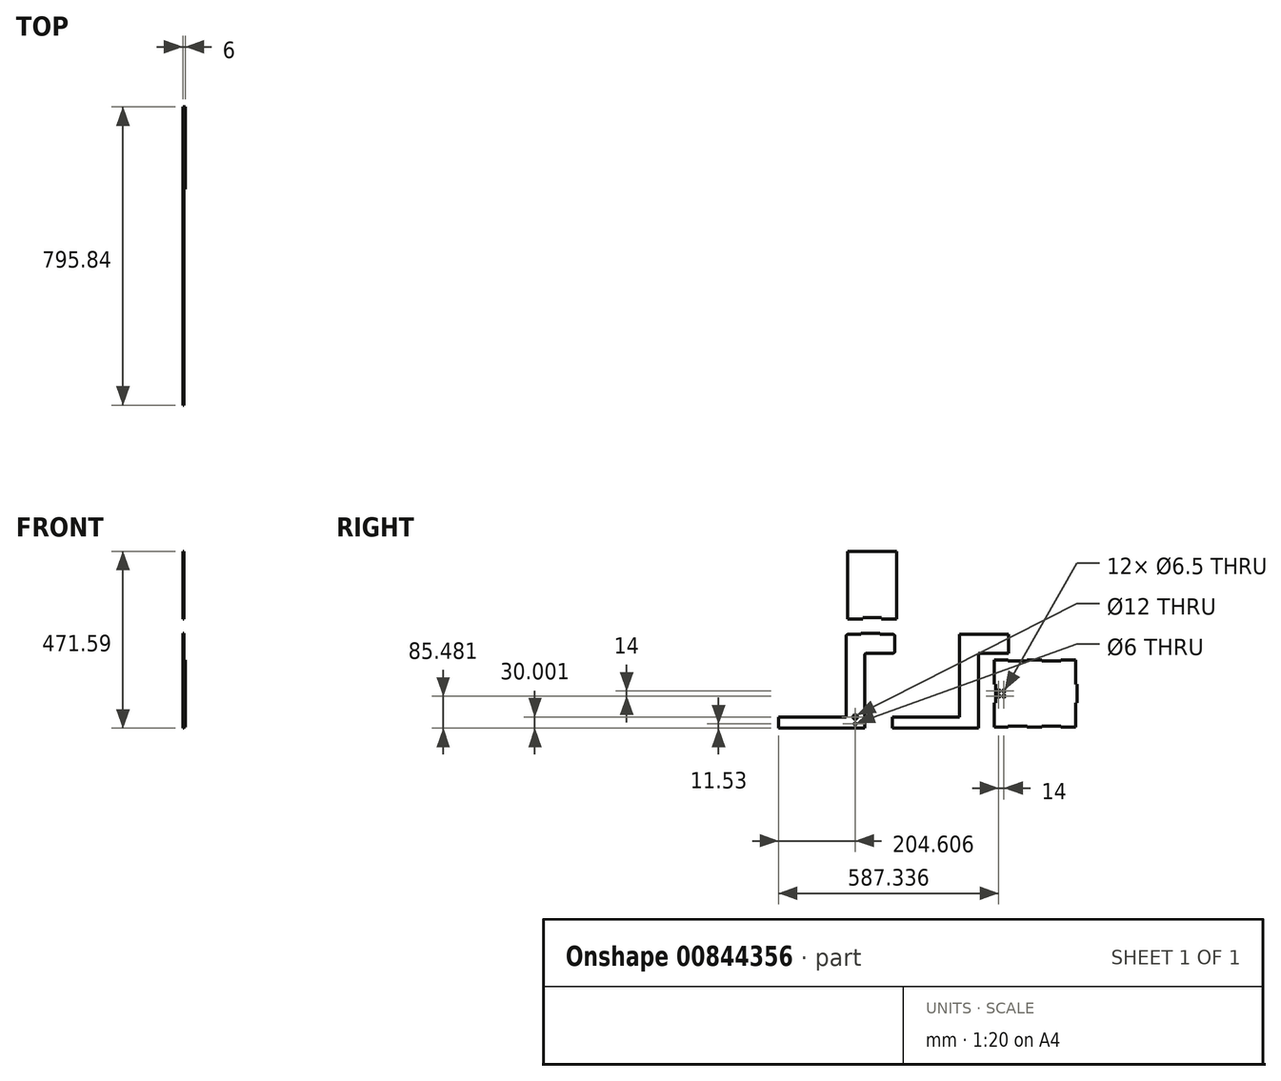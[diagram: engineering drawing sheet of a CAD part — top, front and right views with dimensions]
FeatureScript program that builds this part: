
annotation { "Feature Type Name" : "Feature", "Feature Type Description" : "" }
export const myFeature = defineFeature(function(context is Context, id is Id, definition is map)
    precondition{}
    {
        {
            var Q0;
            Q0=qCreatedBy(makeId("Right.planeOp"),FACE);
            var sketch = newSketch(context, id + "F0", { "sketchPlane" : qUnion([Q0])});
            skLineSegment(sketch, "E0", {"start": v(0, 42.16) * mm, "end": v(130, 42.16) * mm});
            skLineSegment(sketch, "E1", {"start": v(130, 42.16) * mm, "end": v(130, -7.84) * mm});
            skLineSegment(sketch, "E2", {"start": v(50, -7.84) * mm, "end": v(130, -7.84) * mm});
            skLineSegment(sketch, "E3", {"start": v(50, -7.84) * mm, "end": v(50, -207.84) * mm});
            skLineSegment(sketch, "E4", {"start": v(50, -207.84) * mm, "end": v(-180, -207.84) * mm});
            skLineSegment(sketch, "E5", {"start": v(-180, -207.84) * mm, "end": v(-180, -177.84) * mm});
            skLineSegment(sketch, "E6", {"start": v(0, -177.84) * mm, "end": v(-180, -177.84) * mm});
            skLineSegment(sketch, "E7", {"start": v(0, -177.84) * mm, "end": v(0, 42.16) * mm});
            skLineSegment(sketch, "E8", {"start": v(-298.05, 42.16) * mm, "end": v(-263.05, 42.16) * mm});
            skLineSegment(sketch, "E9", {"start": v(-173.05, 37.16) * mm, "end": v(-173.05, -2.84) * mm});
            skLineSegment(sketch, "E10", {"start": v(-248.05, -7.84) * mm, "end": v(-178.05, -7.84) * mm});
            skLineSegment(sketch, "E11", {"start": v(-253.05, -12.84) * mm, "end": v(-253.05, -207.84) * mm});
            skLineSegment(sketch, "E12", {"start": v(-253.05, -207.84) * mm, "end": v(-483.05, -207.84) * mm});
            skLineSegment(sketch, "E13", {"start": v(-483.05, -207.84) * mm, "end": v(-483.05, -177.84) * mm});
            skLineSegment(sketch, "E14", {"start": v(-303.05, -177.84) * mm, "end": v(-483.05, -177.84) * mm});
            skLineSegment(sketch, "E15", {"start": v(-303.05, -177.84) * mm, "end": v(-303.05, 37.16) * mm});
            skCircle(sketch, "E16", {"center": v(-278.44, -177.84) * mm, "radius": 6 * mm});
            skLineSegment(sketch, "E17.bottom", {"start": v(-298.36, 83.75) * mm, "end": v(-258.01, 83.75) * mm});
            skLineSegment(sketch, "E17.top", {"start": v(-298.36, 263.75) * mm, "end": v(-168.36, 263.75) * mm});
            skLineSegment(sketch, "E17.left", {"start": v(-298.36, 83.75) * mm, "end": v(-298.36, 263.75) * mm});
            skLineSegment(sketch, "E17.right", {"start": v(-168.36, 83.75) * mm, "end": v(-168.36, 263.75) * mm});
            skCircle(sketch, "E18", {"center": v(-278.44, -196.31) * mm, "radius": 3 * mm});
            skLineSegment(sketch, "E19", {"start": v(-263.05, 42.16) * mm, "end": v(-263.05, 45.16) * mm});
            skLineSegment(sketch, "E20", {"start": v(-263.05, 45.16) * mm, "end": v(-213.05, 45.16) * mm});
            skLineSegment(sketch, "E21", {"start": v(-213.05, 45.16) * mm, "end": v(-213.05, 42.16) * mm});
            skLineSegment(sketch, "E22.trimOffspring", {"start": v(-213.05, 42.16) * mm, "end": v(-178.05, 42.16) * mm});
            skLineSegment(sketch, "E23.top", {"start": v(-258.01, 86.75) * mm, "end": v(-208.01, 86.75) * mm});
            skLineSegment(sketch, "E23.left", {"start": v(-258.01, 83.75) * mm, "end": v(-258.01, 86.75) * mm});
            skLineSegment(sketch, "E23.right", {"start": v(-208.01, 83.75) * mm, "end": v(-208.01, 86.75) * mm});
            skLineSegment(sketch, "E24.trimOffspring", {"start": v(-208.01, 83.75) * mm, "end": v(-168.36, 83.75) * mm});
            skPoint(sketch, "E25.visualSharp", {"position": v(-303.05, 42.16) * mm});
            skArc(sketch, "E25.filletArc", {"start": v(-298.05, 42.16) * mm, "mid": v(-301.59, 40.7) * mm, "end": v(-303.05, 37.16) * mm});
            skPoint(sketch, "E26.visualSharp", {"position": v(-173.05, 42.16) * mm});
            skArc(sketch, "E26.filletArc", {"start": v(-173.05, 37.16) * mm, "mid": v(-174.52, 40.7) * mm, "end": v(-178.05, 42.16) * mm});
            skPoint(sketch, "E27.visualSharp", {"position": v(-173.05, -7.84) * mm});
            skArc(sketch, "E27.filletArc", {"start": v(-178.05, -7.84) * mm, "mid": v(-174.52, -6.37) * mm, "end": v(-173.05, -2.84) * mm});
            skPoint(sketch, "E28.visualSharp", {"position": v(-253.05, -7.84) * mm});
            skArc(sketch, "E28.filletArc", {"start": v(-248.05, -7.84) * mm, "mid": v(-251.59, -9.3) * mm, "end": v(-253.05, -12.84) * mm});
            skLineSegment(sketch, "E29.bottom", {"start": v(92.79, -25.36) * mm, "end": v(129.79, -25.36) * mm});
            skLineSegment(sketch, "E29.top", {"start": v(92.79, -205.36) * mm, "end": v(129.79, -205.36) * mm});
            skLineSegment(sketch, "E29.right", {"start": v(309.79, -25.36) * mm, "end": v(309.79, -90.36) * mm});
            skLineSegment(sketch, "E30.bottom", {"start": v(309.79, -90.36) * mm, "end": v(312.79, -90.36) * mm});
            skLineSegment(sketch, "E30.top", {"start": v(309.79, -140.36) * mm, "end": v(312.79, -140.36) * mm});
            skLineSegment(sketch, "E30.right", {"start": v(312.79, -90.36) * mm, "end": v(312.79, -140.36) * mm});
            skLineSegment(sketch, "E31.trimOffspring", {"start": v(309.79, -140.36) * mm, "end": v(309.79, -205.36) * mm});
            skLineSegment(sketch, "E32", {"start": v(92.79, -25.36) * mm, "end": v(92.79, -90.36) * mm});
            skPoint(sketch, "E33.top.start.orphan", {"position": v(89.79, -140.36) * mm});
            skLineSegment(sketch, "E34.bottom", {"start": v(92.79, -90.36) * mm, "end": v(95.79, -90.36) * mm});
            skLineSegment(sketch, "E34.top", {"start": v(92.79, -140.36) * mm, "end": v(95.79, -140.36) * mm});
            skLineSegment(sketch, "E34.right", {"start": v(95.79, -90.36) * mm, "end": v(95.79, -140.36) * mm});
            skPoint(sketch, "E33.right.end.orphan", {"position": v(92.79, -140.36) * mm});
            skLineSegment(sketch, "E35.trimOffspring", {"start": v(92.79, -140.36) * mm, "end": v(92.79, -205.36) * mm});
            skLineSegment(sketch, "E36", {"start": v(309.79, -25.36) * mm, "end": v(269.79, -25.36) * mm});
            skLineSegment(sketch, "E37.top", {"start": v(269.79, -28.36) * mm, "end": v(219.79, -28.36) * mm});
            skLineSegment(sketch, "E37.left", {"start": v(269.79, -25.36) * mm, "end": v(269.79, -28.36) * mm});
            skLineSegment(sketch, "E37.right", {"start": v(219.79, -25.36) * mm, "end": v(219.79, -28.36) * mm});
            skLineSegment(sketch, "E38", {"start": v(219.79, -25.36) * mm, "end": v(179.79, -25.36) * mm});
            skLineSegment(sketch, "E39.top", {"start": v(179.79, -28.36) * mm, "end": v(129.79, -28.36) * mm});
            skLineSegment(sketch, "E39.left", {"start": v(179.79, -25.36) * mm, "end": v(179.79, -28.36) * mm});
            skLineSegment(sketch, "E39.right", {"start": v(129.79, -25.36) * mm, "end": v(129.79, -28.36) * mm});
            skLineSegment(sketch, "E40", {"start": v(129.79, -25.36) * mm, "end": v(92.79, -25.36) * mm});
            skLineSegment(sketch, "E41", {"start": v(309.79, -205.36) * mm, "end": v(269.79, -205.36) * mm});
            skLineSegment(sketch, "E42.top", {"start": v(269.79, -202.36) * mm, "end": v(219.79, -202.36) * mm});
            skLineSegment(sketch, "E42.left", {"start": v(269.79, -205.36) * mm, "end": v(269.79, -202.36) * mm});
            skLineSegment(sketch, "E42.right", {"start": v(219.79, -205.36) * mm, "end": v(219.79, -202.36) * mm});
            skLineSegment(sketch, "E43", {"start": v(219.79, -205.36) * mm, "end": v(179.79, -205.36) * mm});
            skLineSegment(sketch, "E44.top", {"start": v(179.79, -202.36) * mm, "end": v(129.79, -202.36) * mm});
            skLineSegment(sketch, "E44.left", {"start": v(179.79, -205.36) * mm, "end": v(179.79, -202.36) * mm});
            skLineSegment(sketch, "E44.right", {"start": v(129.79, -205.36) * mm, "end": v(129.79, -202.36) * mm});
            skLineSegment(sketch, "E45", {"start": v(129.79, -205.36) * mm, "end": v(92.79, -205.36) * mm});
            skLineSegment(sketch, "E46.trimOffspring", {"start": v(179.79, -25.36) * mm, "end": v(219.79, -25.36) * mm});
            skLineSegment(sketch, "E47.trimOffspring", {"start": v(269.79, -25.36) * mm, "end": v(309.79, -25.36) * mm});
            skLineSegment(sketch, "E48.trimOffspring", {"start": v(269.79, -205.36) * mm, "end": v(309.79, -205.36) * mm});
            skLineSegment(sketch, "E49.trimOffspring", {"start": v(179.79, -205.36) * mm, "end": v(219.79, -205.36) * mm});
            skCircle(sketch, "E50", {"center": v(104.29, -108.36) * mm, "radius": 3.25 * mm});
            skCircle(sketch, "E51", {"center": v(118.29, -108.36) * mm, "radius": 3.25 * mm});
            skCircle(sketch, "E52", {"center": v(118.29, -122.36) * mm, "radius": 3.25 * mm});
            skCircle(sketch, "E53", {"center": v(104.29, -122.36) * mm, "radius": 3.25 * mm});
            skPoint(sketch, "E54.start.orphan", {"position": v(111.29, -25.36) * mm});
            skPoint(sketch, "E55.orphan", {"position": v(111.29, -108.36) * mm});
            skPoint(sketch, "E56.orphan", {"position": v(111.29, -115.36) * mm});
            skPoint(sketch, "E57.trimOffspring.end.orphan", {"position": v(111.29, -205.36) * mm});
            skSolve(sketch);
        }
        {
            var Q0;
            Q0=makeQuery(id+"F0.imprint","IMPRINT",FACE,{"disambiguationData":[TD([[makeQuery(id+"F0.imprint","IMPRINT",EDGE,{"derivedFrom":sQuery(id+"F0.wireOp",EDGE,"E0")}),-1.0]])]});
            var Q1;
            Q1=makeQuery(id+"F0.imprint","IMPRINT",FACE,{"disambiguationData":[TD([[makeQuery(id+"F0.imprint","IMPRINT",EDGE,{"derivedFrom":sQuery(id+"F0.wireOp",EDGE,"E8")}),-1.0]])]});
            var Q2;
            Q2=makeQuery(id+"F0.imprint","IMPRINT",FACE,{"disambiguationData":[TD([[makeQuery(id+"F0.imprint","IMPRINT",EDGE,{"derivedFrom":sQuery(id+"F0.wireOp",EDGE,"E17.bottom")}),1.0]])]});
            var Q3;
            Q3=makeQuery(id+"F0.imprint","IMPRINT",FACE,{"disambiguationData":[TD([[makeQuery(id+"F0.imprint","IMPRINT",EDGE,{"derivedFrom":sQuery(id+"F0.wireOp",EDGE,"E29.bottom")}),-1.0]])]});
            extrude(context, id + "F1", {"entities" : qUnion([Q0, Q1, Q2, Q3]), "oppositeDirection" : true, "depth" : 3 * mm, "offsetDistance" : 25 * mm});
        }
        {
            var Q0;
            Q0=makeQuery(id+"F0.imprint","IMPRINT",FACE,{"disambiguationData":[TD([[makeQuery(id+"F0.imprint","IMPRINT",EDGE,{"derivedFrom":sQuery(id+"F0.wireOp",EDGE,"E29.right")}),-1.0]])]});
            extrude(context, id + "F2", {"entities" : qUnion([Q0]), "depth" : 3 * mm, "offsetDistance" : 25 * mm});
        }
        {
            var Q0;
            Q0=makeQuery(id+"F2.opExtrude","SWEPT_BODY",BODY,{"disambiguationData":[OSD([sQuery(id+"F0.wireOp",EDGE,"E29.right"),sQuery(id+"F0.wireOp",EDGE,"E30.bottom"),sQuery(id+"F0.wireOp",EDGE,"E30.top"),sQuery(id+"F0.wireOp",EDGE,"E30.right"),sQuery(id+"F0.wireOp",EDGE,"E31.trimOffspring"),sQuery(id+"F0.wireOp",EDGE,"E32"),sQuery(id+"F0.wireOp",EDGE,"E34.bottom"),sQuery(id+"F0.wireOp",EDGE,"E34.top"),sQuery(id+"F0.wireOp",EDGE,"E34.right"),sQuery(id+"F0.wireOp",EDGE,"E35.trimOffspring"),sQuery(id+"F0.wireOp",EDGE,"E37.top"),sQuery(id+"F0.wireOp",EDGE,"E37.left"),sQuery(id+"F0.wireOp",EDGE,"E37.right"),sQuery(id+"F0.wireOp",EDGE,"E39.top"),sQuery(id+"F0.wireOp",EDGE,"E39.left"),sQuery(id+"F0.wireOp",EDGE,"E39.right"),sQuery(id+"F0.wireOp",EDGE,"E40"),sQuery(id+"F0.wireOp",EDGE,"E42.top"),sQuery(id+"F0.wireOp",EDGE,"E42.left"),sQuery(id+"F0.wireOp",EDGE,"E42.right"),sQuery(id+"F0.wireOp",EDGE,"E44.top"),sQuery(id+"F0.wireOp",EDGE,"E44.left"),sQuery(id+"F0.wireOp",EDGE,"E44.right"),sQuery(id+"F0.wireOp",EDGE,"E45"),sQuery(id+"F0.wireOp",EDGE,"E46.trimOffspring"),sQuery(id+"F0.wireOp",EDGE,"E47.trimOffspring"),sQuery(id+"F0.wireOp",EDGE,"E48.trimOffspring"),sQuery(id+"F0.wireOp",EDGE,"E49.trimOffspring")])]});
            transform(context, id + "F3", {"entities" : qUnion([Q0]), "transformType" : TransformType.TRANSLATION_3D, "dx" : 0 * mm, "dy" : 0 * mm, "dz" : 0 * mm, "makeCopy" : true});
        }
    });
